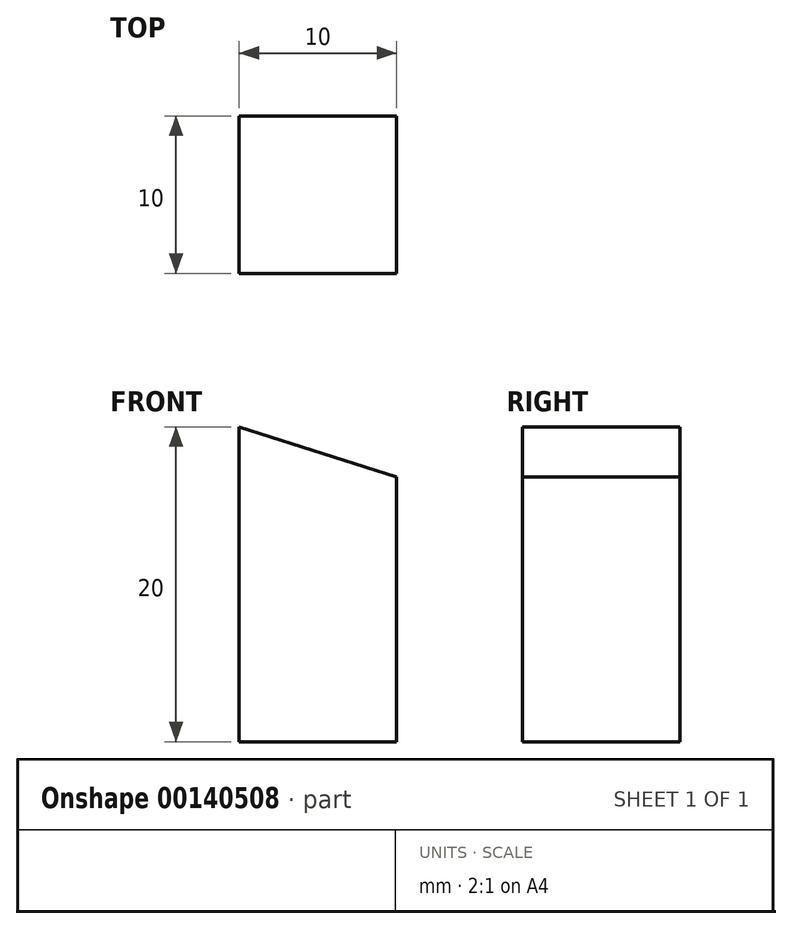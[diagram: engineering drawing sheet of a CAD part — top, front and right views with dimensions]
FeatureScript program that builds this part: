
annotation { "Feature Type Name" : "Feature", "Feature Type Description" : "" }
export const myFeature = defineFeature(function(context is Context, id is Id, definition is map)
    precondition{}
    {
        {
            var Q0;
            Q0=qCreatedBy(makeId("Front.planeOp"),FACE);
            var sketch = newSketch(context, id + "F0", { "sketchPlane" : qUnion([Q0])});
            skLineSegment(sketch, "E0", {"start": v(0, 0) * mm, "end": v(-10, 0) * mm});
            skLineSegment(sketch, "E1", {"start": v(-10, 0) * mm, "end": v(-10, 20) * mm});
            skLineSegment(sketch, "E2", {"start": v(-10, 20) * mm, "end": v(0, 16.8) * mm});
            skLineSegment(sketch, "E3", {"start": v(0, 16.8) * mm, "end": v(0, 0) * mm});
            skSolve(sketch);
        }
        {
            var Q0;
            Q0=makeQuery(id+"F0.imprint","IMPRINT",FACE,{"disambiguationData":[TD([[makeQuery(id+"F0.imprint","IMPRINT",EDGE,{"derivedFrom":sQuery(id+"F0.wireOp",EDGE,"E0")}),-1.0]])]});
            extrude(context, id + "F1", {"entities" : qUnion([Q0]), "depth" : 10 * mm});
        }
    });
